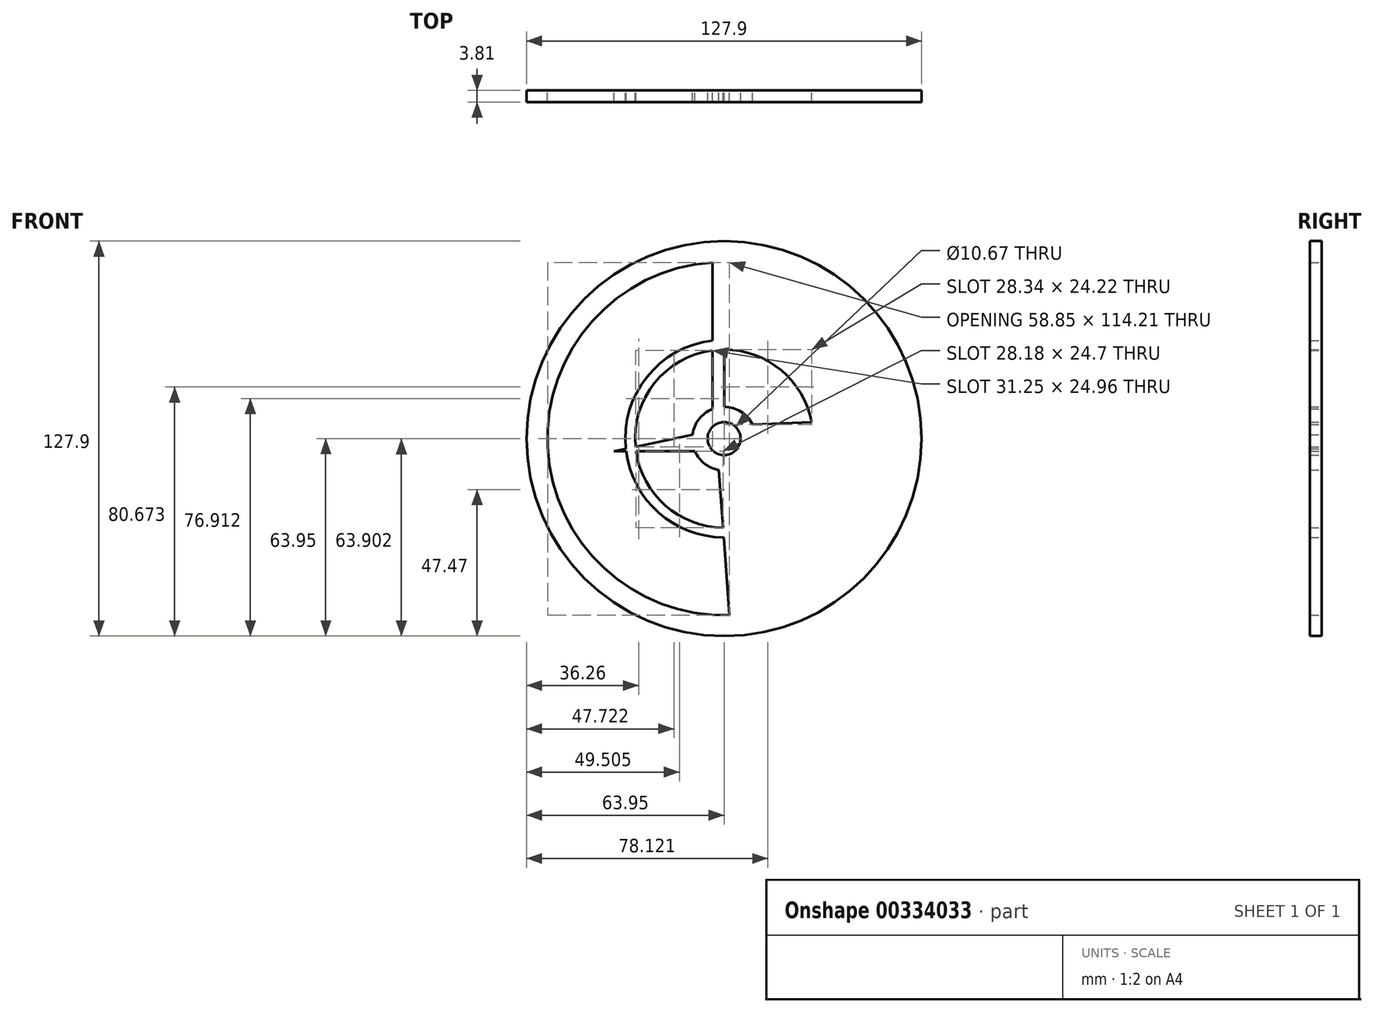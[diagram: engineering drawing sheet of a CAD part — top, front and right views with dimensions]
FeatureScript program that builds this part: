
annotation { "Feature Type Name" : "Feature", "Feature Type Description" : "" }
export const myFeature = defineFeature(function(context is Context, id is Id, definition is map)
    precondition{}
    {
        {
            var Q0;
            Q0=qCreatedBy(makeId("Front.planeOp"),FACE);
            var sketch = newSketch(context, id + "F0", { "sketchPlane" : qUnion([Q0])});
            skCircle(sketch, "E0", {"center": v(0, 0) * mm, "radius": 63.95 * mm});
            skArc(sketch, "E1", {"start": v(-3.75, 57.06) * mm, "mid": v(-44.55, 35.85) * mm, "end": v(-56.54, -8.54) * mm});
            skArc(sketch, "E2", {"start": v(-3.75, 31.77) * mm, "mid": v(-24.98, 19.99) * mm, "end": v(-31.82, -3.32) * mm});
            skArc(sketch, "E3", {"start": v(-3.75, 28.59) * mm, "mid": v(-22.53, 18) * mm, "end": v(-28.7, -2.66) * mm});
            skArc(sketch, "E4", {"start": v(-3.75, 9.58) * mm, "mid": v(-8.13, 6.3) * mm, "end": v(-10.21, 1.25) * mm});
            skCircle(sketch, "E5", {"center": v(0, 0) * mm, "radius": 5.33 * mm});
            skLineSegment(sketch, "E6", {"start": v(-3.75, 9.58) * mm, "end": v(-3.75, 28.59) * mm});
            skLineSegment(sketch, "E7", {"start": v(-3.75, 57.06) * mm, "end": v(0, 57.3) * mm});
            skLineSegment(sketch, "E8", {"start": v(0, 57.3) * mm, "end": v(0, 32) * mm});
            skLineSegment(sketch, "E9.trimOffspring", {"start": v(-3.75, 31.77) * mm, "end": v(-3.75, 57.06) * mm});
            skLineSegment(sketch, "E10.trimOffspring", {"start": v(0, 28.83) * mm, "end": v(0, 9.58) * mm});
            skLineSegment(sketch, "E11", {"start": v(-1.73, -10.14) * mm, "end": v(-0.36, -28.83) * mm});
            skPoint(sketch, "E11.startSnap0", {"position": v(1.73, -10.14) * mm});
            skPoint(sketch, "E11.endSnap0", {"position": v(1.73, -10.14) * mm});
            skLineSegment(sketch, "E12", {"start": v(1.73, -10.14) * mm, "end": v(3.5, -28.62) * mm});
            skArc(sketch, "E13.trimOffspring", {"start": v(1.73, -10.14) * mm, "mid": v(7.86, -6.63) * mm, "end": v(10.29, 0) * mm});
            skArc(sketch, "E14.trimOffspring", {"start": v(3.5, -28.62) * mm, "mid": v(21.59, -19.1) * mm, "end": v(28.83, 0) * mm});
            skArc(sketch, "E15.trimOffspring", {"start": v(3.8, -31.77) * mm, "mid": v(23.93, -21.24) * mm, "end": v(32, 0) * mm});
            skLineSegment(sketch, "E16.trimOffspring", {"start": v(-0.12, -32) * mm, "end": v(1.73, -57.15) * mm});
            skLineSegment(sketch, "E17.trimOffspring", {"start": v(3.8, -31.77) * mm, "end": v(6.2, -56.84) * mm});
            skArc(sketch, "E18.trimOffspring", {"start": v(6.2, -56.84) * mm, "mid": v(57.1, 3.1) * mm, "end": v(0, 57.18) * mm});
            skLineSegment(sketch, "E19", {"start": v(8.84, 4.6) * mm, "end": v(28.34, 5.3) * mm});
            skLineSegment(sketch, "E20", {"start": v(11.48, 0) * mm, "end": v(28.83, 0) * mm});
            skLineSegment(sketch, "E21", {"start": v(-10.21, 1.25) * mm, "end": v(-56.54, -8.54) * mm});
            skPoint(sketch, "E21.startSnap0", {"position": v(-10.21, -1.25) * mm});
            skLineSegment(sketch, "E22", {"start": v(-9.42, -4.13) * mm, "end": v(-57.03, -4.13) * mm});
            skArc(sketch, "E23.trimOffspring", {"start": v(30.76, 8.81) * mm, "mid": v(19.26, 25.55) * mm, "end": v(0, 32) * mm});
            skArc(sketch, "E24.trimOffspring", {"start": v(28.34, 5.3) * mm, "mid": v(18.42, 22.18) * mm, "end": v(0, 28.83) * mm});
            skLineSegment(sketch, "E25.trimOffspring", {"start": v(32, 0) * mm, "end": v(56.98, 0) * mm});
            skLineSegment(sketch, "E26.trimOffspring", {"start": v(30.76, 8.81) * mm, "end": v(56.98, 4.73) * mm});
            skArc(sketch, "E27.trimOffspring", {"start": v(-9.42, -4.13) * mm, "mid": v(-6.34, -8.1) * mm, "end": v(-1.73, -10.14) * mm});
            skArc(sketch, "E28.trimOffspring", {"start": v(-57.03, -4.13) * mm, "mid": v(-38.3, -42.45) * mm, "end": v(1.73, -57.15) * mm});
            skArc(sketch, "E29.trimOffspring", {"start": v(-28.53, -4.13) * mm, "mid": v(-19, -21.68) * mm, "end": v(-0.36, -28.83) * mm});
            skArc(sketch, "E30.trimOffspring", {"start": v(-31.73, -4.13) * mm, "mid": v(-21.16, -24) * mm, "end": v(-0.12, -32) * mm});
            skPoint(sketch, "E31", {"position": v(-8.83, 1.25) * mm});
            skArc(sketch, "E32.trimOffspring", {"start": v(9.2, 4.61) * mm, "mid": v(5.4, 8.75) * mm, "end": v(0, 10.29) * mm});
            skSolve(sketch);
        }
        {
            var Q0;
            Q0 = qSketchRegion(id + "F0", true);
            var Q1;
            {var subQ0=sQuery(id+"F0.wireOp",EDGE,"E23.trimOffspring");Q1=makeQuery(id+"F0.imprint","IMPRINT",FACE,{"disambiguationData":[TD([[makeQuery(id+"F0.imprint","IMPRINT",EDGE,{"derivedFrom":subQ0}),-1.0]])]});}
            extrude(context, id + "F1", {"entities" : qUnion([Q0, Q1]), "depth" : 3.8 * mm});
        }
    });
